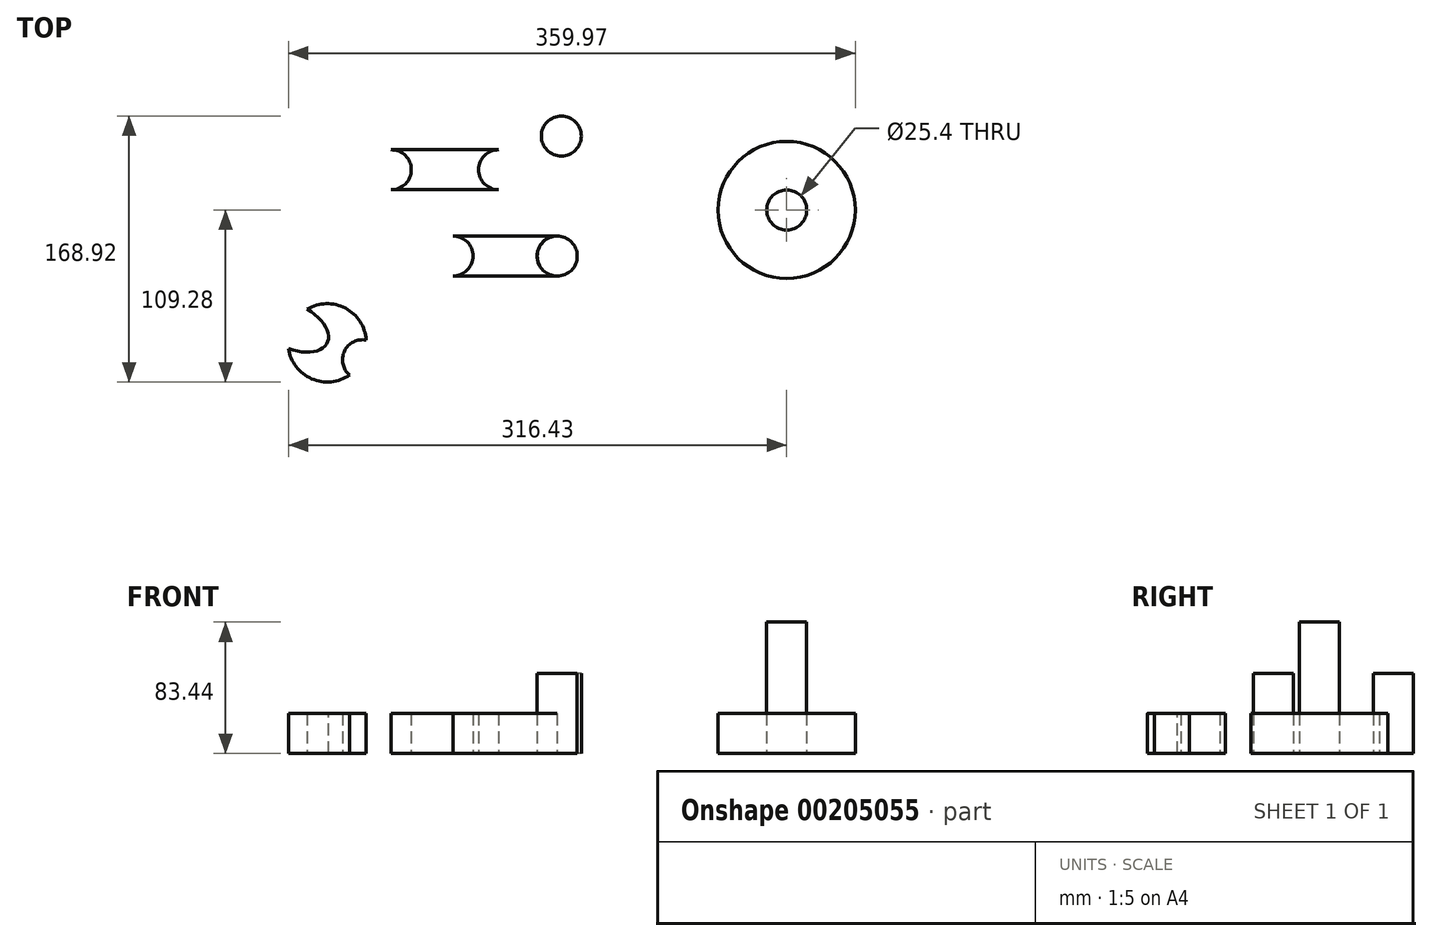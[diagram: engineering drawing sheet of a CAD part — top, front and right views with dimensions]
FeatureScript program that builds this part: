
annotation { "Feature Type Name" : "Feature", "Feature Type Description" : "" }
export const myFeature = defineFeature(function(context is Context, id is Id, definition is map)
    precondition{}
    {
        {
            var Q0;
            Q0=qCreatedBy(makeId("Top.planeOp"),FACE);
            var sketch = newSketch(context, id + "F0", { "sketchPlane" : qUnion([Q0])});
            skCircle(sketch, "E0", {"center": v(0, 0) * mm, "radius": 43.54 * mm});
            skCircle(sketch, "E1", {"center": v(0, 0) * mm, "radius": 12.7 * mm});
            skSolve(sketch);
        }
        {
            var Q0;
            Q0=makeQuery(id+"F0.imprint","IMPRINT",FACE,{"disambiguationData":[TD([[makeQuery(id+"F0.imprint","IMPRINT",EDGE,{"derivedFrom":sQuery(id+"F0.wireOp",EDGE,"E0")}),1.0]])]});
            extrude(context, id + "F1", {"entities" : qUnion([Q0]), "depth" : 25.4 * mm});
        }
        {
            var Q0;
            Q0=qCreatedBy(makeId("Top.planeOp"),FACE);
            var sketch = newSketch(context, id + "F2", { "sketchPlane" : qUnion([Q0])});
            skCircle(sketch, "E2", {"center": v(0, 0) * mm, "radius": 12.7 * mm});
            skSolve(sketch);
        }
        {
            var Q0;
            Q0=makeQuery(id+"F2.imprint","IMPRINT",FACE,{"disambiguationData":[TD([[makeQuery(id+"F2.imprint","IMPRINT",EDGE,{"derivedFrom":sQuery(id+"F2.wireOp",EDGE,"E2")}),1.0]])]});
            var Q1;
            Q1=sQuery(id+"F2.wireOp",EDGE,"E2");
            extrude(context, id + "F3", {"entities" : qUnion([Q0]), "surfaceEntities" : qUnion([Q1]), "depth" : 83.44 * mm});
        }
        {
            var Q0;
            Q0=qCreatedBy(makeId("Top.planeOp"),FACE);
            var sketch = newSketch(context, id + "F4", { "sketchPlane" : qUnion([Q0])});
            skLineSegment(sketch, "E3.bottom", {"start": v(-251.15, 38.24) * mm, "end": v(-182.97, 38.24) * mm});
            skLineSegment(sketch, "E3.top", {"start": v(-251.15, 12.84) * mm, "end": v(-182.97, 12.84) * mm});
            skArc(sketch, "E4", {"start": v(-182.97, 38.24) * mm, "mid": v(-195.67, 25.54) * mm, "end": v(-182.97, 12.84) * mm});
            skArc(sketch, "E5", {"start": v(-251.15, 12.84) * mm, "mid": v(-238.45, 25.54) * mm, "end": v(-251.15, 38.24) * mm});
            skSolve(sketch);
        }
        {
            var Q0;
            Q0=makeQuery(id+"F4.imprint","IMPRINT",FACE,{"disambiguationData":[TD([[makeQuery(id+"F4.imprint","IMPRINT",EDGE,{"derivedFrom":sQuery(id+"F4.wireOp",EDGE,"E3.bottom")}),-1.0]])]});
            extrude(context, id + "F5", {"entities" : qUnion([Q0]), "depth" : 25.4 * mm});
        }
        {
            var Q0;
            Q0=qCreatedBy(makeId("Top.planeOp"),FACE);
            var sketch = newSketch(context, id + "F6", { "sketchPlane" : qUnion([Q0])});
            skCircle(sketch, "E6", {"center": v(-143.13, 46.94) * mm, "radius": 12.7 * mm});
            skSolve(sketch);
        }
        {
            var Q0;
            Q0=makeQuery(id+"F6.imprint","IMPRINT",FACE,{"disambiguationData":[TD([[makeQuery(id+"F6.imprint","IMPRINT",EDGE,{"derivedFrom":sQuery(id+"F6.wireOp",EDGE,"E6")}),1.0]])]});
            extrude(context, id + "F7", {"entities" : qUnion([Q0]), "depth" : 50.8 * mm});
        }
        {
            var Q0;
            Q0=qCreatedBy(makeId("Top.planeOp"),FACE);
            var sketch = newSketch(context, id + "F8", { "sketchPlane" : qUnion([Q0])});
            skLineSegment(sketch, "E7.bottom", {"start": v(-212, -16.5) * mm, "end": v(-145.82, -16.5) * mm});
            skLineSegment(sketch, "E7.top", {"start": v(-212, -41.9) * mm, "end": v(-145.82, -41.9) * mm});
            skArc(sketch, "E8", {"start": v(-145.82, -16.5) * mm, "mid": v(-158.52, -29.2) * mm, "end": v(-145.82, -41.9) * mm});
            skArc(sketch, "E9", {"start": v(-212, -41.9) * mm, "mid": v(-199.3, -29.2) * mm, "end": v(-212, -16.5) * mm});
            skSolve(sketch);
        }
        {
            var Q0;
            Q0=makeQuery(id+"F8.imprint","IMPRINT",FACE,{"disambiguationData":[TD([[makeQuery(id+"F8.imprint","IMPRINT",EDGE,{"derivedFrom":sQuery(id+"F8.wireOp",EDGE,"E7.bottom")}),-1.0]])]});
            extrude(context, id + "F9", {"entities" : qUnion([Q0]), "depth" : 25.4 * mm});
        }
        {
            var Q0;
            Q0=qCreatedBy(makeId("Top.planeOp"),FACE);
            var sketch = newSketch(context, id + "F10", { "sketchPlane" : qUnion([Q0])});
            skCircle(sketch, "E10", {"center": v(-145.74, -29.37) * mm, "radius": 12.7 * mm});
            skSolve(sketch);
        }
        {
            var Q0;
            Q0=makeQuery(id+"F10.imprint","IMPRINT",FACE,{"disambiguationData":[TD([[makeQuery(id+"F10.imprint","IMPRINT",EDGE,{"derivedFrom":sQuery(id+"F10.wireOp",EDGE,"E10")}),1.0]])]});
            extrude(context, id + "F11", {"entities" : qUnion([Q0]), "depth" : 50.8 * mm});
        }
        {
            var Q0;
            Q0=qCreatedBy(makeId("Top.planeOp"),FACE);
            var sketch = newSketch(context, id + "F12", { "sketchPlane" : qUnion([Q0])});
            skArc(sketch, "E11", {"start": v(-316.43, -88.01) * mm, "mid": v(-301.72, -107.24) * mm, "end": v(-277.63, -104.82) * mm});
            skEllipticalArc(sketch, "E12", {});
            skArc(sketch, "E13", {"start": v(-267.04, -82.67) * mm, "mid": v(-280.87, -89.67) * mm, "end": v(-277.63, -104.82) * mm});
            skArc(sketch, "E14.trimOffspring", {"start": v(-267.04, -82.67) * mm, "mid": v(-280.3, -62.41) * mm, "end": v(-304.5, -63.04) * mm});
            const initialGuessF12  = {"E12": [-0.31426166991821136, -0.07371234782922409, 0.9022904937427817, -0.4311285943908236, 0.024855969116122385, 0.014038679801755423, 4.882462180516844, 1.4007231266627422]};
            skSetInitialGuess(sketch, initialGuessF12);
            skSolve(sketch);
        }
        {
            var Q0;
            Q0=makeQuery(id+"F12.imprint","IMPRINT",FACE,{"disambiguationData":[TD([[makeQuery(id+"F12.imprint","IMPRINT",EDGE,{"derivedFrom":sQuery(id+"F12.wireOp",EDGE,"E11")}),1.0]])]});
            extrude(context, id + "F13", {"entities" : qUnion([Q0]), "depth" : 25.4 * mm});
        }
    });
